# Revit family: NBS_Allermuir_OffcChrs_AxylStool
name_source: partatom
category: Furniture
revit_build: Autodesk Revit 2016 (Build: 20151007_0715(x64)
units: mm (PartAtom-declared; Revit-internal decimal feet)

## family parameters
Always vertical = Yes
Cut with Voids When Loaded = No
Room Calculation Point = No
Shared = No
Work Plane-Based = No

## types (2) — shared parameters
AssetType = Moveable
Category = Pr_40_50_12_57:Office chairs
DurationUnit = year
ExpectedLife = 5
FootHeight = 5 mm  [stored 0.0164042 ft]
FrameColour = Black, white, sage, basalt, peacock blue, coral, pebble, stone, polished aluminium, raw aluminium
FrameFinishOptions = Powder coat, polished aluminium, raw aluminium
FrameMaterials = Aluminium
FrameMountingMaterial = NBS_Concept
IfcExportAs = IfcFurnitureType
IfcExportType = CHAIR
IsBuiltIn = No
LegHeight = 377 mm  [stored 1.23688 ft]
ManufacturerName = Allermuir
ManufacturerURL = www.senator.co.uk
Material = Aluminium
ModelReference = Axyl
NBSCertification = www.nationalbimlibrary.com/cert/xqm5rrz0
NBSDescription = Office chairs
NBSReference = 45-35-20/330
NominalDepth = 495 mm
NominalHeight = 645 mm
NominalLength = 465 mm  [stored 1.52559 ft]
NominalWidth = 495 mm
OptionalFeatures = Glides with felt
SeatFrameMaterial = NBS_Concept
SeatingSeatMaterial = NBS_Concept
SeatsAndBacksColour = Black, white, sage, basalt, peacock blue, coral (plastic); pebble, stone (wood fibre)
SeatsAndBacksMaterial = Plastic
SeatsAndBacksMaterialOptions = Plastic, Wood fibre injected plastic
StandardsDurability = BS EN 16139
StandardsSafetyRequirements = BS EN 16139, BS EN 1022:2005
Status = UNSET
Uniclass2015Code = Pr_40_50_12_57
Uniclass2015Title = Office chairs
Uniclass2015Version = Products v1.9
Version = 1
WarrantyDescription = Allermuir warrant that its manufactured products are free from manufacturing defects - in materials or workmanship - for a period of five (5) years. , Allermuir will repair, or replace (at Allermuir's sole discretion) with comparable free of charge materials / components, any product / component which fails under normal use in a single shift environment, as a result of a defect in the materials and/ or workmanship
WarrantyDurationParts = 5
WarrantyDurationUnit = year
zero-valued in all types: HighestSeatingHeight, LowestSeatingHeight

## per-type parameters (varying)
| type | BIMObjectName | Description | Features | Name | SeatingHeight | Size |
| AXL03 | NBS_Allermuir_OfficeChairs_Axyl_AXL03 | Stool | Integral plastic footrest protectors, Plastic glides | OfficeChairs_Axyl_AXL03_Allermuir | 645 mm | 465 x 495 x 645 mm |
| AXL04 | NBS_Allermuir_OfficeChairs_Axyl_AXL04 | High stool | Integral plastic footrest protectors, Plastic Glides | OfficeChairs_Axyl_AXL04_Allermuir | 750 mm | 465 x 495 x 750 mm |

note: column(s) folded — value = type name in every type: ModelNumber

note: [stored X ft] marks values corroborated as IEEE doubles in the binary element streams (Revit-internal decimal feet)

## geometry (parser evidence)
native form markers: Sweep x7
no freeform markers — native parametric forms only
